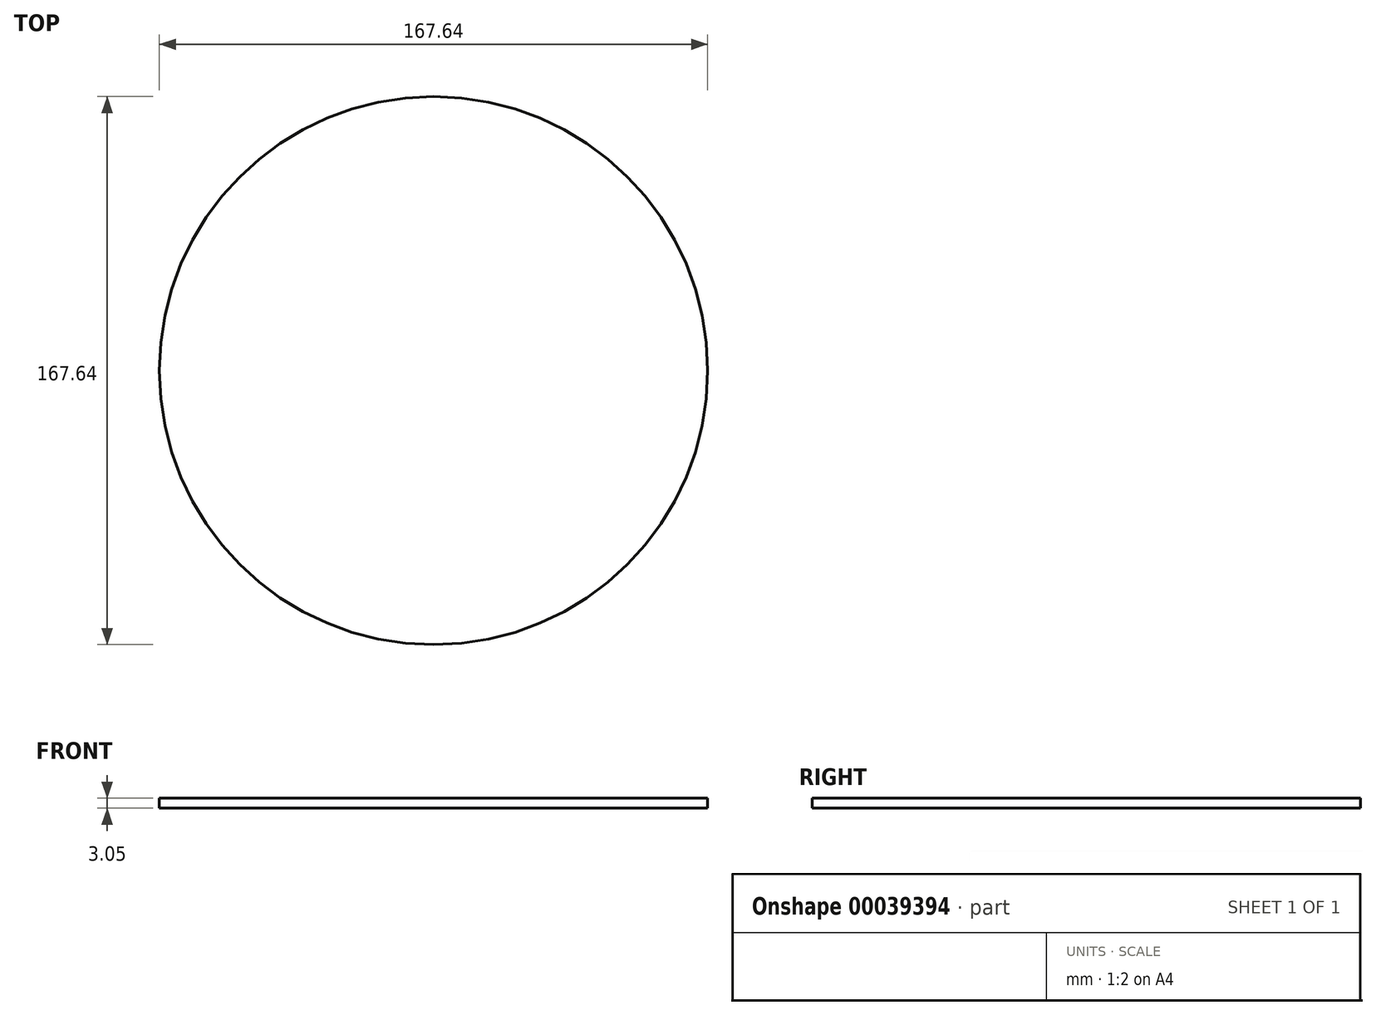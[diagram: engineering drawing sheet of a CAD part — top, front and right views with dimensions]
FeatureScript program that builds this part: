
annotation { "Feature Type Name" : "Feature", "Feature Type Description" : "" }
export const myFeature = defineFeature(function(context is Context, id is Id, definition is map)
    precondition{}
    {
        {
            var Q0;
            Q0=qCreatedBy(makeId("Top.planeOp"),FACE);
            var sketch = newSketch(context, id + "F0", { "sketchPlane" : qUnion([Q0])});
            skCircle(sketch, "E0", {"center": v(0, 0) * mm, "radius": 83.82 * mm});
            skSolve(sketch);
        }
        {
            var Q0;
            Q0 = qSketchRegion(id + "F0", true);
            extrude(context, id + "F1", {"entities" : qUnion([Q0]), "depth" : 3.05 * mm});
        }
    });
